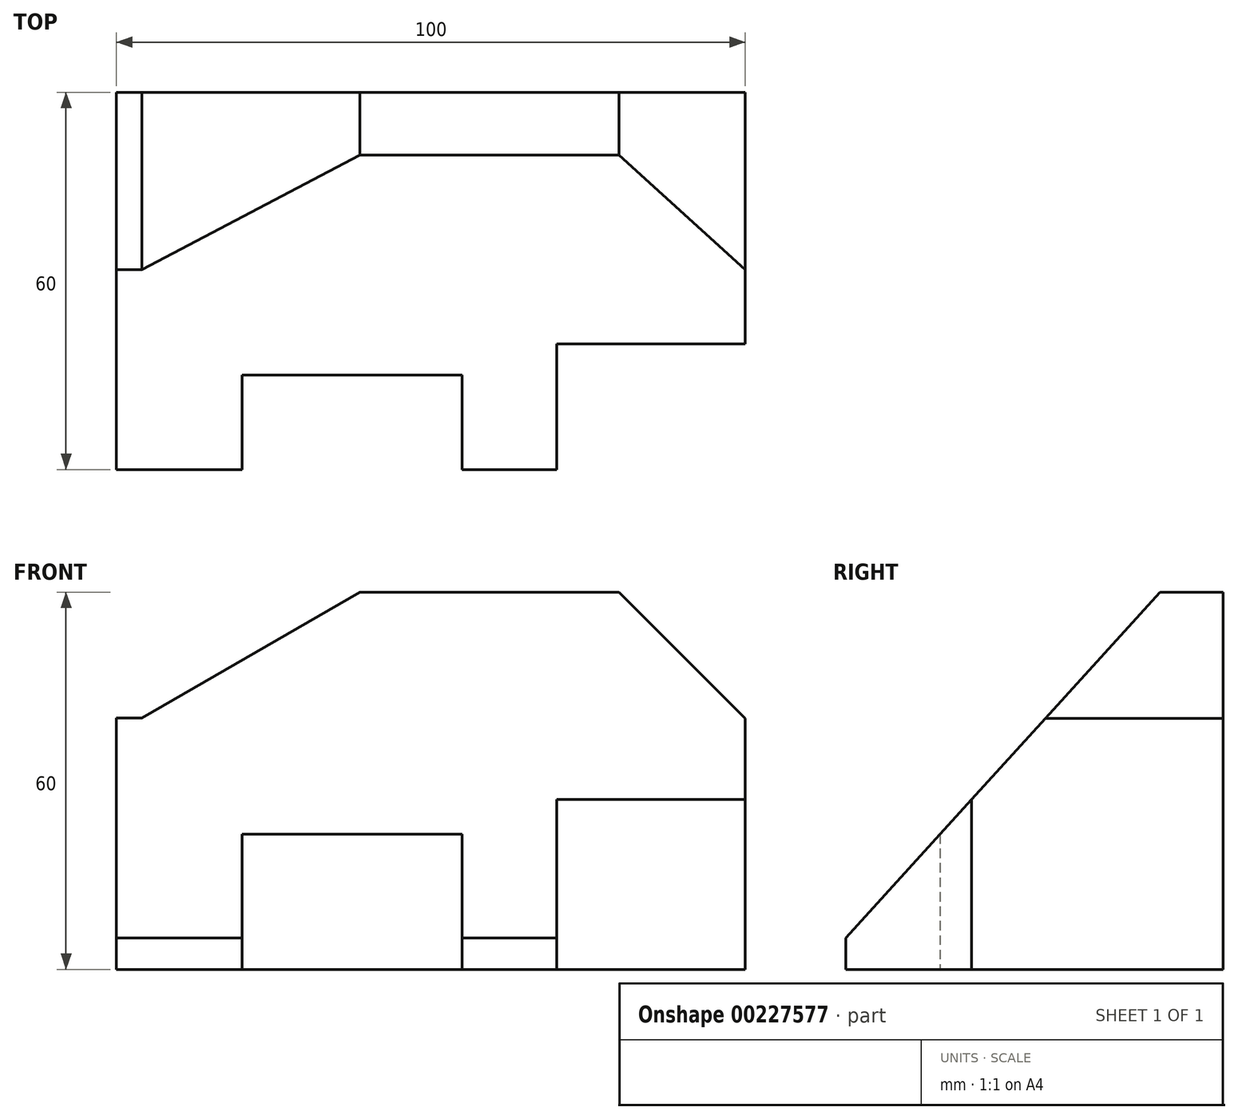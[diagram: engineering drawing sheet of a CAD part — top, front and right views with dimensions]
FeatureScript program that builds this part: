
annotation { "Feature Type Name" : "Feature", "Feature Type Description" : "" }
export const myFeature = defineFeature(function(context is Context, id is Id, definition is map)
    precondition{}
    {
        {
            var Q0;
            Q0=qCreatedBy(makeId("Top.planeOp"),FACE);
            var sketch = newSketch(context, id + "F0", { "sketchPlane" : qUnion([Q0])});
            skLineSegment(sketch, "E0", {"start": v(0, 0) * mm, "end": v(0, 40) * mm});
            skLineSegment(sketch, "E1", {"start": v(0, 0) * mm, "end": v(20, 0) * mm});
            skLineSegment(sketch, "E2", {"start": v(20, 0) * mm, "end": v(20, 15) * mm});
            skLineSegment(sketch, "E3", {"start": v(20, 15) * mm, "end": v(55, 15) * mm});
            skLineSegment(sketch, "E4", {"start": v(55, 15) * mm, "end": v(55, 0) * mm});
            skLineSegment(sketch, "E5", {"start": v(55, 0) * mm, "end": v(70, 0) * mm});
            skLineSegment(sketch, "E6", {"start": v(70, 0) * mm, "end": v(70, 20) * mm});
            skLineSegment(sketch, "E7", {"start": v(70, 20) * mm, "end": v(100, 20) * mm});
            skLineSegment(sketch, "E8", {"start": v(100, 20) * mm, "end": v(100, 40) * mm});
            skLineSegment(sketch, "E9", {"start": v(100, 40) * mm, "end": v(0, 40) * mm});
            skSolve(sketch);
        }
        {
            var Q0;
            Q0 = qSketchRegion(id + "F0", true);
            extrude(context, id + "F1", {"entities" : qUnion([Q0]), "depth" : 60 * mm});
        }
        {
            var Q0;
            Q0=makeQuery(id+"F1.opExtrude","SWEPT_FACE",FACE,{"disambiguationData":[OSD([sQuery(id+"F0.wireOp",EDGE,"E9")])]});
            extrude(context, id + "F2", {"entities" : qUnion([Q0]), "operationType" : NewBodyOperationType.ADD, "depth" : 20 * mm});
        }
        {
            var Q0;
            Q0=qCreatedBy(makeId("Right.planeOp"),FACE);
            var sketch = newSketch(context, id + "F3", { "sketchPlane" : qUnion([Q0])});
            skLineSegment(sketch, "E10.0", {"start": v(20, 60) * mm, "end": v(60, 60) * mm});
            skLineSegment(sketch, "E11.0", {"start": v(20, 60) * mm, "end": v(0, 60) * mm});
            skLineSegment(sketch, "E12", {"start": v(60, 60) * mm, "end": v(50, 60) * mm});
            skLineSegment(sketch, "E13", {"start": v(0, 0) * mm, "end": v(0, 5) * mm});
            skLineSegment(sketch, "E14", {"start": v(0, 5) * mm, "end": v(50, 60) * mm});
            skLineSegment(sketch, "E15", {"start": v(50, 60) * mm, "end": v(0, 60) * mm});
            skLineSegment(sketch, "E16", {"start": v(0, 5) * mm, "end": v(0, 60) * mm});
            skSolve(sketch);
        }
        {
            var Q0;
            Q0=makeQuery(id+"F3.imprint","IMPRINT",FACE,{"disambiguationData":[TD([[makeQuery(id+"F3.imprint","IMPRINT",EDGE,{"derivedFrom":sQuery(id+"F3.wireOp",EDGE,"E14")}),1.0]])]});
            extrude(context, id + "F4", {"entities" : qUnion([Q0]), "operationType" : NewBodyOperationType.REMOVE, "endBound" : BoundingType.THROUGH_ALL, "depth" : 25 * mm});
        }
        {
            var Q0;
            Q0=qCreatedBy(makeId("Front.planeOp"),FACE);
            var sketch = newSketch(context, id + "F5", { "sketchPlane" : qUnion([Q0])});
            skLineSegment(sketch, "E17.0.0", {"start": v(20, 5) * mm, "end": v(20, 21.5) * mm});
            skLineSegment(sketch, "E17.0.1", {"start": v(20, 21.5) * mm, "end": v(55, 21.5) * mm});
            skLineSegment(sketch, "E17.0.2", {"start": v(55, 21.5) * mm, "end": v(55, 5) * mm});
            skLineSegment(sketch, "E17.0.3", {"start": v(55, 5) * mm, "end": v(70, 5) * mm});
            skLineSegment(sketch, "E17.0.4", {"start": v(70, 5) * mm, "end": v(70, 27) * mm});
            skLineSegment(sketch, "E17.0.5", {"start": v(70, 27) * mm, "end": v(100, 27) * mm});
            skLineSegment(sketch, "E17.0.6", {"start": v(100, 27) * mm, "end": v(100, 60) * mm});
            skLineSegment(sketch, "E17.0.7", {"start": v(100, 60) * mm, "end": v(0, 60) * mm});
            skLineSegment(sketch, "E17.0.8", {"start": v(0, 60) * mm, "end": v(0, 5) * mm});
            skLineSegment(sketch, "E17.0.9", {"start": v(0, 5) * mm, "end": v(20, 5) * mm});
            skLineSegment(sketch, "E18", {"start": v(0, 0) * mm, "end": v(0, 40) * mm});
            skLineSegment(sketch, "E19", {"start": v(0, 40) * mm, "end": v(4.04, 40) * mm});
            skLineSegment(sketch, "E20", {"start": v(4.04, 40) * mm, "end": v(38.69, 60) * mm});
            skLineSegment(sketch, "E21", {"start": v(100, 39.94) * mm, "end": v(79.94, 60) * mm});
            skSolve(sketch);
        }
        {
            var Q0;
            {var subQ0=sQuery(id+"F5.wireOp",EDGE,"E17.0.8");Q0=makeQuery(id+"F5.imprint","IMPRINT",FACE,{"disambiguationData":[TD([[makeQuery(id+"F5.imprint","IMPRINT",EDGE,{"derivedFrom":subQ0}),1.0]])]});}
            var Q1;
            {var subQ3=sQuery(id+"F5.wireOp",EDGE,"E21");Q1=makeQuery(id+"F5.imprint","IMPRINT",FACE,{"disambiguationData":[TD([[makeQuery(id+"F5.imprint","IMPRINT",EDGE,{"derivedFrom":subQ3}),-1.0]])]});}
            extrude(context, id + "F6", {"entities" : qUnion([Q0, Q1]), "operationType" : NewBodyOperationType.REMOVE, "endBound" : BoundingType.THROUGH_ALL, "oppositeDirection" : true, "depth" : 25 * mm});
        }
    });
